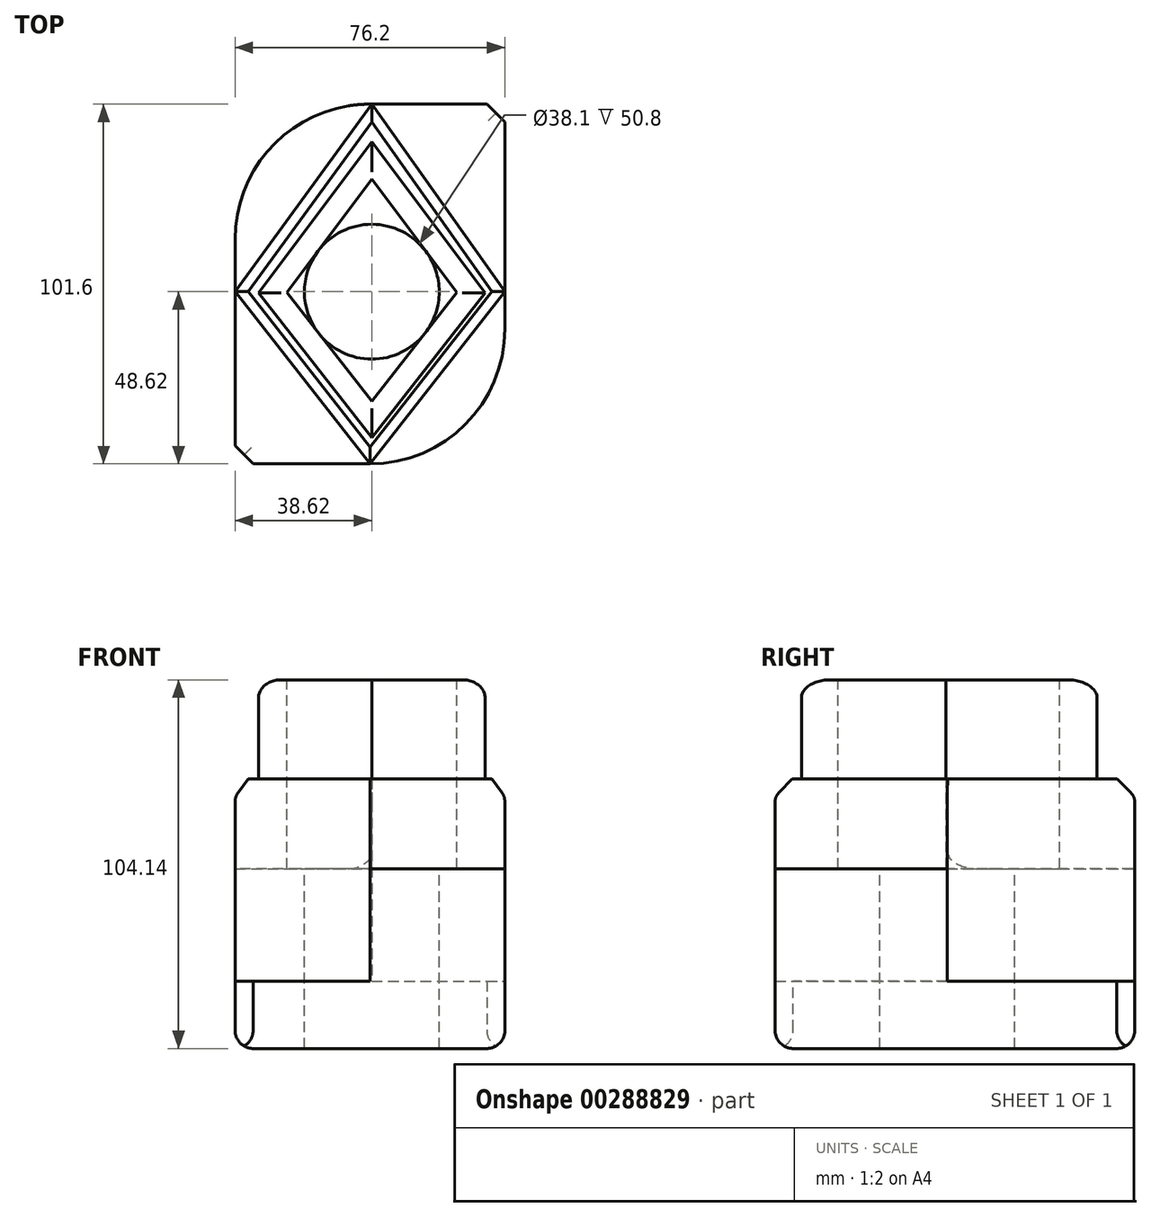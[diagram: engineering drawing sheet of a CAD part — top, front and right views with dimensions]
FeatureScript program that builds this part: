
annotation { "Feature Type Name" : "Feature", "Feature Type Description" : "" }
export const myFeature = defineFeature(function(context is Context, id is Id, definition is map)
    precondition{}
    {
        {
            var Q0;
            Q0=qCreatedBy(makeId("Top.planeOp"),FACE);
            var sketch = newSketch(context, id + "F0", { "sketchPlane" : qUnion([Q0])});
            skLineSegment(sketch, "E0.bottom", {"start": v(-0.52, 52.98) * mm, "end": v(37.58, 52.98) * mm});
            skLineSegment(sketch, "E0.top", {"start": v(-38.62, -48.62) * mm, "end": v(-0.52, -48.62) * mm});
            skLineSegment(sketch, "E0.left", {"start": v(-38.62, 14.88) * mm, "end": v(-38.62, -48.62) * mm});
            skLineSegment(sketch, "E0.right", {"start": v(37.58, 52.98) * mm, "end": v(37.58, -10.52) * mm});
            skPoint(sketch, "E1.visualSharp", {"position": v(-38.62, 52.98) * mm});
            skArc(sketch, "E1.filletArc", {"start": v(-0.52, 52.98) * mm, "mid": v(-27.46, 41.82) * mm, "end": v(-38.62, 14.88) * mm});
            skPoint(sketch, "E2.bottom.end.orphan", {"position": v(-25.92, 0) * mm});
            skPoint(sketch, "E3.right.start.orphan", {"position": v(12.18, 0) * mm});
            skPoint(sketch, "E4.visualSharp", {"position": v(37.58, -48.62) * mm});
            skArc(sketch, "E4.filletArc", {"start": v(-0.52, -48.62) * mm, "mid": v(26.42, -37.46) * mm, "end": v(37.58, -10.52) * mm});
            skLineSegment(sketch, "E5", {"start": v(0, 52.98) * mm, "end": v(37.58, 0) * mm});
            skLineSegment(sketch, "E6", {"start": v(-0.52, -48.62) * mm, "end": v(-38.62, 0) * mm});
            skSolve(sketch);
        }
        {
            var Q0;
            {var subQ0=sQuery(id+"F0.wireOp",EDGE,"E1.filletArc");Q0=makeQuery(id+"F0.imprint","IMPRINT",FACE,{"disambiguationData":[TD([[makeQuery(id+"F0.imprint","IMPRINT",EDGE,{"derivedFrom":subQ0}),1.0]])]});}
            extrude(context, id + "F1", {"entities" : qUnion([Q0]), "depth" : 50.8 * mm});
        }
        {
            var Q0;
            {var subQ0=sQuery(id+"F0.wireOp",EDGE,"E0.top");Q0=makeQuery(id+"F0.imprint","IMPRINT",FACE,{"disambiguationData":[TD([[makeQuery(id+"F0.imprint","IMPRINT",EDGE,{"derivedFrom":subQ0}),1.0]])]});}
            var Q1;
            {var subQ3=sQuery(id+"F0.wireOp",EDGE,"E5");Q1=makeQuery(id+"F0.imprint","IMPRINT",FACE,{"disambiguationData":[TD([[makeQuery(id+"F0.imprint","IMPRINT",EDGE,{"derivedFrom":subQ3}),1.0]])]});}
            extrude(context, id + "F2", {"entities" : qUnion([Q0, Q1]), "operationType" : NewBodyOperationType.ADD, "depth" : 19.05 * mm});
        }
        {
            var Q0;
            Q0=makeQuery(id+"F1.opExtrude","CAP_FACE",FACE,{"disambiguationData":[OSD([sQuery(id+"F0.wireOp",EDGE,"E0.bottom"),sQuery(id+"F0.wireOp",EDGE,"E0.left"),sQuery(id+"F0.wireOp",EDGE,"E0.right"),sQuery(id+"F0.wireOp",EDGE,"E1.filletArc"),sQuery(id+"F0.wireOp",EDGE,"E4.filletArc"),sQuery(id+"F0.wireOp",EDGE,"E5"),sQuery(id+"F0.wireOp",EDGE,"E6")])],"isStart":false});
            var sketch = newSketch(context, id + "F3", { "sketchPlane" : qUnion([Q0])});
            skLineSegment(sketch, "E7", {"start": v(-38.62, 0) * mm, "end": v(0, 52.98) * mm});
            skLineSegment(sketch, "E8", {"start": v(37.58, 0) * mm, "end": v(-0.52, -48.62) * mm});
            skLineSegment(sketch, "E9", {"start": v(-38.62, 0) * mm, "end": v(37.58, 0) * mm});
            skSolve(sketch);
        }
        {
            var Q0;
            Q0=makeQuery(id+"F3.imprint","IMPRINT",FACE,{"disambiguationData":[TD([[makeQuery(id+"F3.imprint","IMPRINT",EDGE,{"derivedFrom":sQuery(id+"F3.wireOp",EDGE,"E7")}),-1.0]])]});
            extrude(context, id + "F4", {"entities" : qUnion([Q0]), "operationType" : NewBodyOperationType.ADD, "depth" : 25.4 * mm});
        }
        {
            var Q0;
            {var subQ0=sQuery(id+"F0.wireOp",EDGE,"E6");var subQ1=sQuery(id+"F0.wireOp",EDGE,"E5");var subQ2=sQuery(id+"F0.wireOp",EDGE,"E4.filletArc");var subQ3=sQuery(id+"F0.wireOp",EDGE,"E0.right");var subQ4=sQuery(id+"F0.wireOp",EDGE,"E0.left");var subQ5=makeQuery(id+"F1.opExtrude","CAP_FACE",FACE,{"disambiguationData":[OSD([sQuery(id+"F0.wireOp",EDGE,"E0.bottom"),subQ4,subQ3,sQuery(id+"F0.wireOp",EDGE,"E1.filletArc"),subQ2,subQ1,subQ0])],"isStart":false});Q0=makeQuery(id+"F4.boolean.opBoolean","SPLIT",FACE,{"disambiguationData":[TD([makeQuery(id+"F1.opExtrude","SWEPT_FACE",FACE,{"disambiguationData":[OSD([subQ3])]})])],"derivedFrom":subQ5});}
            var sketch = newSketch(context, id + "F5", { "sketchPlane" : qUnion([Q0])});
            skLineSegment(sketch, "E10", {"start": v(37.58, 0) * mm, "end": v(-0.52, -48.62) * mm});
            skSolve(sketch);
        }
        {
            var Q0;
            Q0=makeQuery(id+"F5.imprint","IMPRINT",FACE,{"disambiguationData":[TD([[makeQuery(id+"F5.imprint","IMPRINT",EDGE,{"derivedFrom":sQuery(id+"F5.wireOp",EDGE,"E10")}),-1.0]])]});
            extrude(context, id + "F6", {"entities" : qUnion([Q0]), "operationType" : NewBodyOperationType.ADD, "depth" : 25.4 * mm});
        }
        {
            var Q0;
            {var subQ0=sQuery(id+"F3.wireOp",EDGE,"E9");Q0=makeQuery(id+"F6.boolean.opBoolean","MERGE",FACE,{"derivedFrom":[makeQuery(id+"F4.opExtrude","CAP_FACE",FACE,{"disambiguationData":[OSD([sQuery(id+"F0.wireOp",EDGE,"E5"),sQuery(id+"F3.wireOp",EDGE,"E7"),subQ0])],"isStart":false}),makeQuery(id+"F6.opExtrude","CAP_FACE",FACE,{"disambiguationData":[OSD([sQuery(id+"F0.wireOp",EDGE,"E6"),subQ0,sQuery(id+"F5.wireOp",EDGE,"E10")])],"isStart":false})]});}
            var sketch = newSketch(context, id + "F7", { "sketchPlane" : qUnion([Q0])});
            skCircle(sketch, "E11", {"center": v(0, 0) * mm, "radius": 19.05 * mm});
            skSolve(sketch);
        }
        {
            var Q0;
            Q0=makeQuery(id+"F7.imprint","IMPRINT",FACE,{"disambiguationData":[TD([[makeQuery(id+"F7.imprint","IMPRINT",EDGE,{"derivedFrom":sQuery(id+"F7.wireOp",EDGE,"E11")}),1.0]])]});
            extrude(context, id + "F8", {"entities" : qUnion([Q0]), "operationType" : NewBodyOperationType.REMOVE, "endBound" : BoundingType.THROUGH_ALL, "oppositeDirection" : true, "depth" : 25.4 * mm});
        }
        {
            var Q0;
            Q0=makeQuery(id+"F6.opExtrude","CAP_EDGE",EDGE,{"disambiguationData":[OSD([sQuery(id+"F5.wireOp",EDGE,"E10")])],"isStart":false});
            var Q1;
            Q1=makeQuery(id+"F6.opExtrude","CAP_EDGE",EDGE,{"disambiguationData":[OSD([sQuery(id+"F0.wireOp",EDGE,"E6")])],"isStart":false});
            chamfer(context, id + "F9", {"entities" : qUnion([Q0, Q1]), "chamferType" : ChamferType.OFFSET_ANGLE, "width" : 5.08 * mm, "oppositeDirection" : false, "angle" : 30 * degree, "tangentPropagation" : true});
        }
        {
            var Q0;
            Q0=makeQuery(id+"F4.opExtrude","CAP_EDGE",EDGE,{"disambiguationData":[OSD([sQuery(id+"F3.wireOp",EDGE,"E7")])],"isStart":false});
            var Q1;
            Q1=makeQuery(id+"F4.opExtrude","CAP_EDGE",EDGE,{"disambiguationData":[OSD([sQuery(id+"F0.wireOp",EDGE,"E5")])],"isStart":false});
            chamfer(context, id + "F10", {"entities" : qUnion([Q0, Q1]), "chamferType" : ChamferType.OFFSET_ANGLE, "width" : 5.08 * mm, "oppositeDirection" : false, "angle" : 30 * degree, "tangentPropagation" : true});
        }
        {
            var Q0;
            Q0=makeQuery(id+"F2.opExtrude","CAP_EDGE",EDGE,{"disambiguationData":[OSD([sQuery(id+"F0.wireOp",EDGE,"E6")])],"isStart":false});
            var Q1;
            Q1=makeQuery(id+"F2.opExtrude","CAP_EDGE",EDGE,{"disambiguationData":[OSD([sQuery(id+"F0.wireOp",EDGE,"E5")])],"isStart":false});
            var Q2;
            Q2=makeQuery(id+"F6.opExtrude","CAP_EDGE",EDGE,{"disambiguationData":[OSD([sQuery(id+"F5.wireOp",EDGE,"E10")])],"isStart":true});
            var Q3;
            Q3=makeQuery(id+"F4.opExtrude","CAP_EDGE",EDGE,{"disambiguationData":[OSD([sQuery(id+"F3.wireOp",EDGE,"E7")])],"isStart":true});
            fillet(context, id + "F11", {"entities" : qUnion([Q0, Q1, Q2, Q3]), "radius" : 5.08 * mm, "tangentPropagation" : true, "allowEdgeOverflow" : false});
        }
        {
            var Q0;
            Q0=makeQuery(id+"F2.opExtrude","SWEPT_EDGE",EDGE,{"disambiguationData":[OSD([sQuery(id+"F0.wireOp",EDGE,"E0.bottom"),sQuery(id+"F0.wireOp",EDGE,"E0.right")])]});
            var Q1;
            Q1=makeQuery(id+"F2.opExtrude","SWEPT_EDGE",EDGE,{"disambiguationData":[OSD([sQuery(id+"F0.wireOp",EDGE,"E0.top"),sQuery(id+"F0.wireOp",EDGE,"E0.left")])]});
            chamfer(context, id + "F12", {"entities" : qUnion([Q0, Q1]), "width" : 5.08 * mm, "tangentPropagation" : true});
        }
        {
            var Q0;
            Q0=makeQuery(id+"F2.opExtrude","CAP_EDGE",EDGE,{"disambiguationData":[OSD([sQuery(id+"F0.wireOp",EDGE,"E0.top")])],"isStart":true});
            var Q1;
            {var subQ0=sQuery(id+"F0.wireOp",EDGE,"E0.left");Q1=makeQuery(id+"F2.boolean.opBoolean","MERGE",EDGE,{"derivedFrom":[makeQuery(id+"F1.opExtrude","CAP_EDGE",EDGE,{"disambiguationData":[OSD([subQ0])],"isStart":true}),makeQuery(id+"F2.opExtrude","CAP_EDGE",EDGE,{"disambiguationData":[OSD([subQ0])],"isStart":true})]});}
            fillet(context, id + "F13", {"entities" : qUnion([Q0, Q1]), "radius" : 5.08 * mm, "tangentPropagation" : true, "allowEdgeOverflow" : false});
        }
        {
            var Q0;
            {var subQ0=sQuery(id+"F3.wireOp",EDGE,"E9");Q0=makeQuery(id+"F6.boolean.opBoolean","MERGE",FACE,{"derivedFrom":[makeQuery(id+"F4.opExtrude","CAP_FACE",FACE,{"disambiguationData":[OSD([sQuery(id+"F0.wireOp",EDGE,"E5"),sQuery(id+"F3.wireOp",EDGE,"E7"),subQ0])],"isStart":false}),makeQuery(id+"F6.opExtrude","CAP_FACE",FACE,{"disambiguationData":[OSD([sQuery(id+"F0.wireOp",EDGE,"E6"),subQ0,sQuery(id+"F5.wireOp",EDGE,"E10")])],"isStart":false})]});}
            var sketch = newSketch(context, id + "F14", { "sketchPlane" : qUnion([Q0])});
            skLineSegment(sketch, "E12", {"start": v(0, 31.75) * mm, "end": v(-24, -0.25) * mm});
            skLineSegment(sketch, "E13", {"start": v(-24.2, 0) * mm, "end": v(0, -30.88) * mm});
            skLineSegment(sketch, "E14", {"start": v(0, -30.88) * mm, "end": v(24.2, 0) * mm});
            skLineSegment(sketch, "E15", {"start": v(24, -0.25) * mm, "end": v(0, 31.75) * mm});
            skSolve(sketch);
        }
        {
            var Q0;
            {var subQ0=sQuery(id+"F14.wireOp",EDGE,"E15");var subQ1=sQuery(id+"F14.wireOp",EDGE,"E14");var subQ2=makeQuery(id+"F14.imprint","INTERSECT",VERTEX,{"derivedFrom":[subQ1,subQ0]});Q0=makeQuery(id+"F14.imprint","IMPRINT",FACE,{"disambiguationData":[TD([[makeQuery(id+"F14.imprint","IMPRINT",EDGE,{"disambiguationData":[TD([[subQ2,1.0]])],"derivedFrom":subQ1}),1.0]])]});}
            var Q1;
            {var subQ0=sQuery(id+"F14.wireOp",EDGE,"E15");var subQ1=sQuery(id+"F14.wireOp",EDGE,"E12");var subQ2=makeQuery(id+"F14.imprint","INTERSECT",VERTEX,{"derivedFrom":[subQ1,subQ0]});Q1=makeQuery(id+"F14.imprint","IMPRINT",FACE,{"disambiguationData":[TD([[makeQuery(id+"F14.imprint","IMPRINT",EDGE,{"disambiguationData":[TD([[subQ2,-1.0]])],"derivedFrom":subQ1}),1.0]])]});}
            var Q2;
            {var subQ0=sQuery(id+"F14.wireOp",EDGE,"E14");var subQ1=sQuery(id+"F14.wireOp",EDGE,"E13");var subQ2=makeQuery(id+"F14.imprint","INTERSECT",VERTEX,{"derivedFrom":[subQ1,subQ0]});Q2=makeQuery(id+"F14.imprint","IMPRINT",FACE,{"disambiguationData":[TD([[makeQuery(id+"F14.imprint","IMPRINT",EDGE,{"disambiguationData":[TD([[subQ2,1.0]])],"derivedFrom":subQ1}),1.0]])]});}
            var Q3;
            {var subQ0=sQuery(id+"F14.wireOp",EDGE,"E13");var subQ1=sQuery(id+"F14.wireOp",EDGE,"E12");var subQ2=makeQuery(id+"F14.imprint","INTERSECT",VERTEX,{"derivedFrom":[subQ1,subQ0]});Q3=makeQuery(id+"F14.imprint","IMPRINT",FACE,{"disambiguationData":[TD([[makeQuery(id+"F14.imprint","IMPRINT",EDGE,{"disambiguationData":[TD([[subQ2,1.0]])],"derivedFrom":subQ1}),1.0]])]});}
            extrude(context, id + "F15", {"entities" : qUnion([Q0, Q1, Q2, Q3]), "operationType" : NewBodyOperationType.REMOVE, "oppositeDirection" : true, "depth" : 25.4 * mm});
        }
        {
            var Q0;
            {var subQ0=sQuery(id+"F3.wireOp",EDGE,"E9");Q0=makeQuery(id+"F6.boolean.opBoolean","MERGE",FACE,{"derivedFrom":[makeQuery(id+"F4.opExtrude","CAP_FACE",FACE,{"disambiguationData":[OSD([sQuery(id+"F0.wireOp",EDGE,"E5"),sQuery(id+"F3.wireOp",EDGE,"E7"),subQ0])],"isStart":false}),makeQuery(id+"F6.opExtrude","CAP_FACE",FACE,{"disambiguationData":[OSD([sQuery(id+"F0.wireOp",EDGE,"E6"),subQ0,sQuery(id+"F5.wireOp",EDGE,"E10")])],"isStart":false})]});}
            var sketch = newSketch(context, id + "F16", { "sketchPlane" : qUnion([Q0])});
            skLineSegment(sketch, "E16.0", {"start": v(0, 42.33) * mm, "end": v(-32, -0.34) * mm});
            skLineSegment(sketch, "E16.1", {"start": v(32, -0.34) * mm, "end": v(0, 42.33) * mm});
            skLineSegment(sketch, "E16.2", {"start": v(0, -41.18) * mm, "end": v(32, -0.34) * mm});
            skLineSegment(sketch, "E16.3", {"start": v(-32, -0.34) * mm, "end": v(0, -41.18) * mm});
            skSolve(sketch);
        }
        {
            var Q0;
            Q0=makeQuery(id+"F16.imprint","IMPRINT",FACE,{"disambiguationData":[TD([[makeQuery(id+"F16.imprint","IMPRINT",EDGE,{"derivedFrom":sQuery(id+"F16.wireOp",EDGE,"E16.0")}),1.0]])]});
            extrude(context, id + "F17", {"entities" : qUnion([Q0]), "operationType" : NewBodyOperationType.ADD, "depth" : 27.94 * mm});
        }
        {
            var Q0;
            Q0=makeQuery(id+"F17.opExtrude","CAP_EDGE",EDGE,{"disambiguationData":[OSD([sQuery(id+"F16.wireOp",EDGE,"E16.3")])],"isStart":false});
            var Q1;
            Q1=makeQuery(id+"F17.opExtrude","CAP_EDGE",EDGE,{"disambiguationData":[OSD([sQuery(id+"F16.wireOp",EDGE,"E16.0")])],"isStart":false});
            var Q2;
            Q2=makeQuery(id+"F17.opExtrude","CAP_EDGE",EDGE,{"disambiguationData":[OSD([sQuery(id+"F16.wireOp",EDGE,"E16.2")])],"isStart":false});
            var Q3;
            Q3=makeQuery(id+"F17.opExtrude","CAP_EDGE",EDGE,{"disambiguationData":[OSD([sQuery(id+"F16.wireOp",EDGE,"E16.1")])],"isStart":false});
            var Q4;
            {var subQ0=sQuery(id+"F0.wireOp",EDGE,"E6");Q4=makeQuery(id+"F9.opChamfer","BLEND_EDGE",EDGE,{"blendedFrom":[makeQuery(id+"F6.opExtrude","CAP_EDGE",EDGE,{"disambiguationData":[OSD([subQ0])],"isStart":false}),makeQuery(id+"F6.boolean.opBoolean","MERGE",FACE,{"derivedFrom":[makeQuery(id+"F1.opExtrude","SWEPT_FACE",FACE,{"disambiguationData":[OSD([subQ0])]}),makeQuery(id+"F6.opExtrude","SWEPT_FACE",FACE,{"disambiguationData":[OSD([subQ0])]})]})],"blendedInto":[makeQuery(id+"F6.boolean.opBoolean","MERGE",FACE,{"derivedFrom":[makeQuery(id+"F1.opExtrude","SWEPT_FACE",FACE,{"disambiguationData":[OSD([subQ0])]}),makeQuery(id+"F6.opExtrude","SWEPT_FACE",FACE,{"disambiguationData":[OSD([subQ0])]})]})]});}
            var Q5;
            {var subQ0=sQuery(id+"F3.wireOp",EDGE,"E7");Q5=makeQuery(id+"F10.opChamfer","BLEND_EDGE",EDGE,{"blendedFrom":[makeQuery(id+"F4.opExtrude","CAP_EDGE",EDGE,{"disambiguationData":[OSD([subQ0])],"isStart":false}),makeQuery(id+"F4.opExtrude","SWEPT_FACE",FACE,{"disambiguationData":[OSD([subQ0])]})],"blendedInto":[makeQuery(id+"F4.opExtrude","SWEPT_FACE",FACE,{"disambiguationData":[OSD([subQ0])]})]});}
            var Q6;
            {var subQ0=sQuery(id+"F0.wireOp",EDGE,"E5");Q6=makeQuery(id+"F10.opChamfer","BLEND_EDGE",EDGE,{"blendedFrom":[makeQuery(id+"F4.opExtrude","CAP_EDGE",EDGE,{"disambiguationData":[OSD([subQ0])],"isStart":false}),makeQuery(id+"F4.boolean.opBoolean","MERGE",FACE,{"derivedFrom":[makeQuery(id+"F1.opExtrude","SWEPT_FACE",FACE,{"disambiguationData":[OSD([subQ0])]}),makeQuery(id+"F4.opExtrude","SWEPT_FACE",FACE,{"disambiguationData":[OSD([subQ0])]})]})],"blendedInto":[makeQuery(id+"F4.boolean.opBoolean","MERGE",FACE,{"derivedFrom":[makeQuery(id+"F1.opExtrude","SWEPT_FACE",FACE,{"disambiguationData":[OSD([subQ0])]}),makeQuery(id+"F4.opExtrude","SWEPT_FACE",FACE,{"disambiguationData":[OSD([subQ0])]})]})]});}
            var Q7;
            {var subQ0=sQuery(id+"F5.wireOp",EDGE,"E10");Q7=makeQuery(id+"F9.opChamfer","BLEND_EDGE",EDGE,{"blendedFrom":[makeQuery(id+"F6.opExtrude","CAP_EDGE",EDGE,{"disambiguationData":[OSD([subQ0])],"isStart":false}),makeQuery(id+"F6.opExtrude","SWEPT_FACE",FACE,{"disambiguationData":[OSD([subQ0])]})],"blendedInto":[makeQuery(id+"F6.opExtrude","SWEPT_FACE",FACE,{"disambiguationData":[OSD([subQ0])]})]});}
            fillet(context, id + "F18", {"entities" : qUnion([Q0, Q1, Q2, Q3, Q4, Q5, Q6, Q7]), "radius" : 5.08 * mm, "tangentPropagation" : true, "allowEdgeOverflow" : false});
        }
    });
